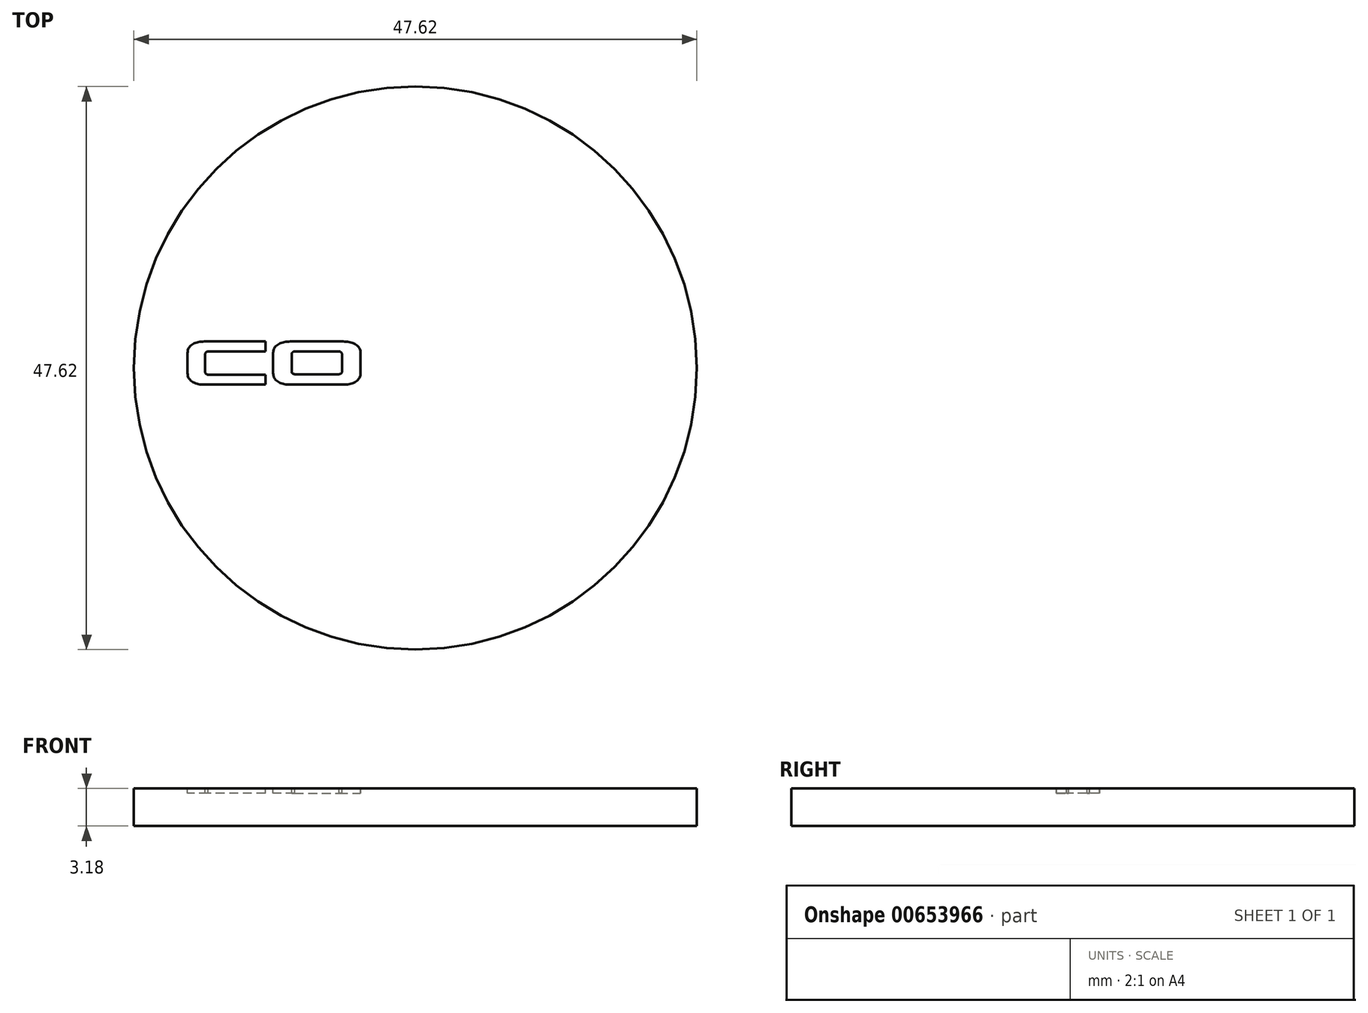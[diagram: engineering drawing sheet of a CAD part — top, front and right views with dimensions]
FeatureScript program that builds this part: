
annotation { "Feature Type Name" : "Feature", "Feature Type Description" : "" }
export const myFeature = defineFeature(function(context is Context, id is Id, definition is map)
    precondition{}
    {
        {
            var Q0;
            Q0=qCreatedBy(makeId("Top.planeOp"),FACE);
            var sketch = newSketch(context, id + "F0", { "sketchPlane" : qUnion([Q0])});
            skCircle(sketch, "E0", {"center": v(0, 0) * mm, "radius": 23.81 * mm});
            skSolve(sketch);
        }
        {
            var Q0;
            Q0=makeQuery(id+"F0.imprint","IMPRINT",FACE,{"disambiguationData":[TD([[makeQuery(id+"F0.imprint","IMPRINT",EDGE,{"derivedFrom":sQuery(id+"F0.wireOp",EDGE,"E0")}),1.0]])]});
            extrude(context, id + "F1", {"entities" : qUnion([Q0]), "depth" : 3.17 * mm, "offsetDistance" : 25.4 * mm});
        }
        {
            var Q0;
            Q0=makeQuery(id+"F1.opExtrude","CAP_FACE",FACE,{"disambiguationData":[OSD([sQuery(id+"F0.wireOp",EDGE,"E0")])],"isStart":false});
            var sketch = newSketch(context, id + "F2", { "sketchPlane" : qUnion([Q0])});
            skLineSegment(sketch, "E1.bottom", {"start": v(-12.7, 2.25) * mm, "end": v(-17.54, 2.25) * mm});
            skLineSegment(sketch, "E1.top", {"start": v(-12.7, 1.4) * mm, "end": v(-17.54, 1.4) * mm});
            skLineSegment(sketch, "E1.left", {"start": v(-12.7, 2.25) * mm, "end": v(-12.7, 1.4) * mm});
            skLineSegment(sketch, "E2.left", {"start": v(-17.8, 1.15) * mm, "end": v(-17.8, -0.3) * mm});
            skLineSegment(sketch, "E2.right", {"start": v(-19.27, 1.15) * mm, "end": v(-19.27, -0.3) * mm});
            skLineSegment(sketch, "E3.bottom", {"start": v(-12.7, -0.56) * mm, "end": v(-17.54, -0.56) * mm});
            skLineSegment(sketch, "E3.top", {"start": v(-12.7, -1.4) * mm, "end": v(-17.54, -1.4) * mm});
            skLineSegment(sketch, "E3.left", {"start": v(-12.7, -0.56) * mm, "end": v(-12.7, -1.4) * mm});
            skLineSegment(sketch, "E4", {"start": v(-17.54, 2.43) * mm, "end": v(-17.54, 2.25) * mm, "construction": true});
            skArc(sketch, "E5", {"start": v(-17.8, 1.15) * mm, "mid": v(-17.72, 1.33) * mm, "end": v(-17.54, 1.4) * mm});
            skArc(sketch, "E6", {"start": v(-17.8, -0.3) * mm, "mid": v(-17.72, -0.49) * mm, "end": v(-17.54, -0.56) * mm});
            skFitSpline(sketch, "E7", {"points": [v(-17.54, 2.25) * mm, v(-17.93, 2.25) * mm, v(-18.44, 2.18) * mm, v(-18.87, 2) * mm, v(-19.13, 1.76) * mm, v(-19.23, 1.55) * mm, v(-19.27, 1.32) * mm, v(-19.27, 1.15) * mm], "startDerivative": vector(-2.24, 0.04) * mm, "endDerivative": vector(0, -1.55) * mm});
            skLineSegment(sketch, "E8", {"start": v(-19.27, 0.42) * mm, "end": v(-17.8, 0.42) * mm, "construction": true});
            skFitSpline(sketch, "E9.MirrorCS", {"points": [v(-17.54, -1.4) * mm, v(-17.93, -1.4) * mm, v(-18.44, -1.34) * mm, v(-18.87, -1.15) * mm, v(-19.13, -0.91) * mm, v(-19.23, -0.7) * mm, v(-19.27, -0.48) * mm, v(-19.27, -0.3) * mm], "startDerivative": vector(-2.24, -0.04) * mm, "endDerivative": vector(0, 1.55) * mm});
            skLineSegment(sketch, "E10.trimOffspring", {"start": v(-17.54, 1.4) * mm, "end": v(-17.54, -0.3) * mm, "construction": true});
            skLineSegment(sketch, "E11.trimOffspring", {"start": v(-17.54, -1.4) * mm, "end": v(-17.54, -1.58) * mm, "construction": true});
            skSolve(sketch);
        }
        {
            var Q0;
            Q0=makeQuery(id+"F2.imprint","IMPRINT",FACE,{"disambiguationData":[TD([[makeQuery(id+"F2.imprint","IMPRINT",EDGE,{"derivedFrom":sQuery(id+"F2.wireOp",EDGE,"E1.bottom")}),1.0]])]});
            extrude(context, id + "F3", {"entities" : qUnion([Q0]), "operationType" : NewBodyOperationType.REMOVE, "oppositeDirection" : true, "depth" : 0.4 * mm, "offsetDistance" : 25.4 * mm});
        }
        {
            var Q0;
            Q0=makeQuery(id+"F2.imprint","IMPRINT",FACE,{"disambiguationData":[TD([[makeQuery(id+"F2.imprint","IMPRINT",EDGE,{"derivedFrom":sQuery(id+"F2.wireOp",EDGE,"E1.bottom")}),-1.0]])]});
            var sketch = newSketch(context, id + "F4", { "sketchPlane" : qUnion([Q0])});
            skLineSegment(sketch, "E12.bottom", {"start": v(-10.2, 1.41) * mm, "end": v(-6.46, 1.41) * mm});
            skLineSegment(sketch, "E12.top", {"start": v(-10.2, 2.25) * mm, "end": v(-6.46, 2.25) * mm});
            skLineSegment(sketch, "E12.right", {"start": v(-6.46, 1.41) * mm, "end": v(-6.46, 2.25) * mm});
            skLineSegment(sketch, "E13.left", {"start": v(-10.46, 1.2) * mm, "end": v(-10.46, -0.35) * mm});
            skLineSegment(sketch, "E13.right", {"start": v(-12.03, 1.15) * mm, "end": v(-12.03, -0.3) * mm});
            skLineSegment(sketch, "E14.left", {"start": v(-4.64, 1.15) * mm, "end": v(-4.64, -0.3) * mm});
            skLineSegment(sketch, "E14.right", {"start": v(-6.2, 1.2) * mm, "end": v(-6.2, -0.36) * mm});
            skLineSegment(sketch, "E15.bottom", {"start": v(-10.2, -1.4) * mm, "end": v(-6.46, -1.4) * mm});
            skLineSegment(sketch, "E15.top", {"start": v(-10.2, -0.52) * mm, "end": v(-6.46, -0.52) * mm});
            skArc(sketch, "E16", {"start": v(-10.2, 1.41) * mm, "mid": v(-10.37, 1.35) * mm, "end": v(-10.46, 1.2) * mm});
            skArc(sketch, "E17", {"start": v(-10.46, -0.35) * mm, "mid": v(-10.36, -0.47) * mm, "end": v(-10.2, -0.52) * mm});
            skArc(sketch, "E18", {"start": v(-6.46, -0.52) * mm, "mid": v(-6.31, -0.47) * mm, "end": v(-6.2, -0.36) * mm});
            skArc(sketch, "E19", {"start": v(-6.2, 1.2) * mm, "mid": v(-6.3, 1.35) * mm, "end": v(-6.46, 1.41) * mm});
            skFitSpline(sketch, "E20", {"points": [v(-10.2, 2.25) * mm, v(-10.7, 2.24) * mm, v(-11.2, 2.18) * mm, v(-11.62, 2) * mm, v(-11.9, 1.76) * mm, v(-12, 1.55) * mm, v(-12.03, 1.33) * mm, v(-12.03, 1.15) * mm], "startDerivative": vector(-2.24, 0.04) * mm, "endDerivative": vector(0, -1.55) * mm});
            skLineSegment(sketch, "E21", {"start": v(-8.34, 2.25) * mm, "end": v(-8.34, -1.4) * mm, "construction": true});
            skPoint(sketch, "E21.endSnap0", {"position": v(-8.34, -1.4) * mm});
            skFitSpline(sketch, "E22.MirrorCS", {"points": [v(-6.46, 2.25) * mm, v(-5.97, 2.24) * mm, v(-5.48, 2.18) * mm, v(-5.05, 2) * mm, v(-4.78, 1.76) * mm, v(-4.68, 1.55) * mm, v(-4.64, 1.33) * mm, v(-4.64, 1.15) * mm], "startDerivative": vector(2.24, 0.04) * mm, "endDerivative": vector(0, -1.55) * mm});
            skLineSegment(sketch, "E23", {"start": v(-12.03, 0.42) * mm, "end": v(-10.46, 0.42) * mm, "construction": true});
            skLineSegment(sketch, "E24", {"start": v(-6.2, 0.42) * mm, "end": v(-4.64, 0.42) * mm, "construction": true});
            skFitSpline(sketch, "E25.MirrorCS", {"points": [v(-10.2, -1.4) * mm, v(-10.7, -1.4) * mm, v(-11.2, -1.33) * mm, v(-11.62, -1.15) * mm, v(-11.9, -0.9) * mm, v(-12, -0.7) * mm, v(-12.03, -0.48) * mm, v(-12.03, -0.3) * mm], "startDerivative": vector(-2.24, -0.04) * mm, "endDerivative": vector(0, 1.55) * mm});
            skFitSpline(sketch, "E26.MirrorCS", {"points": [v(-6.46, -1.4) * mm, v(-5.97, -1.4) * mm, v(-5.48, -1.33) * mm, v(-5.05, -1.15) * mm, v(-4.78, -0.9) * mm, v(-4.68, -0.7) * mm, v(-4.64, -0.48) * mm, v(-4.64, -0.3) * mm], "startDerivative": vector(2.24, -0.04) * mm, "endDerivative": vector(0, 1.55) * mm});
            skPoint(sketch, "E27.orphan", {"position": v(-12.03, -0.35) * mm});
            skSolve(sketch);
        }
        {
            var Q0;
            Q0 = qSketchRegion(id + "F4", true);
            extrude(context, id + "F5", {"entities" : qUnion([Q0]), "operationType" : NewBodyOperationType.REMOVE, "oppositeDirection" : true, "depth" : 0.4 * mm, "offsetDistance" : 25.4 * mm});
        }
    });
